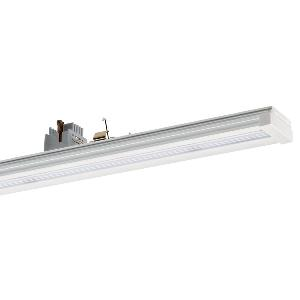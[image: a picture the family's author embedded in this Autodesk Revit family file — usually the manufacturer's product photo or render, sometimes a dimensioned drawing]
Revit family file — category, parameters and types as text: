
# Revit family: conveo_-_cvg_8000_850_xn-p_ea_5_226848229-00804960_20da
name_source: partatom
category: Lighting Fixtures
units: mm (PartAtom-declared; Revit-internal decimal feet)

## family parameters
Cut with Voids When Loaded = No
Host = Face
Light Source = No
Part Type = Normal
Room Calculation Point = No
Round Connector Dimension = Use Diameter
Shared = No

## types (1)
- CONVEO - CVG 8000/850/xN-P/EA/5 (1 x LED, 7800 lm, 5000K)
    Apparent Load = 55 VA
    Approval mark = CE
    CIE Flux Codes = 57 84 97 100 100
    Color Rendering = 80-89
    Color Temperature = 5000K
    Control Gear = Electronic ballast
    Default Elevation = 1800 mm
    Description = CVG 8000/850/xN-P/EA/5|Continuous-row system|light source: LED|work equipment: Electronic ballast|connected load: 220-240 V, 50-60 Hz|Power consumption: approx. 55 W|luminous flux: 7800 lm|luminous efficacy: 141 lm/W|colour temperature: Cold white, ca. 5000 K|color rendering index (CRI): >= 80|chromaticity tolerance:  3 SDCM|System of protection: IP 54|class of protection: I|technology: Switchable|luminaire body|material: Aluminium|surface: Powder coatet|colour: White|lamp cover: Acrylic (PMMA), Satine|weight (net): approx. 1.9 kg|Fastening: Available separately|minimum ambient temperature: -25 ░C|maximum ambient temperature: 47 ░C|glare control: Prism optics (linear)|Approval mark: VDE - ENEC|
    Frequency = 50 Hz
    Height = 70 mm
    Lamp = 1 x LED
    Lamp Light Flux = 7800 lm
    Lamp count = 1
    Length = 1500 mm
    Luminous efficacy = 142 lm/W
    Manufacturer = Waldmann
    ModVariant = No
    Model = 226848229-00804960
    Mounting Place = Ceiling
    Mounting Type = Pendant
    Number of Poles = 1
    OnlyDefault = Yes
    Power Factor = 1
    Product Name = CONVEO - CVG 8000/850/xN-P/EA/5
    Product group = Continuous-row system (industry)
    ProductGroupID = 301
    Protection Class = Protection class I
    Protection Degree = IP 54
    RLX_Detail_Level = 1
    RlxData = <blob elided: 100241 chars, md5=2d86c9af>
    Socket = socket
    Standby Power = 0 W
    System Light Flux = 7800 lm
    System Power = 55 W
    Type Comments = Product without accessories
    Type Image = 226848079-00804943-1p5.jpg
    URL = http://relux.com
    VarID = ---
    Voltage = 230 V
    Voltage Range = 220-240 V
    Weight = 0.00 kg
    Width = 64 mm

## geometry (parser evidence)
native form markers: Blend x4, Sweep x10
no freeform markers — native parametric forms only
